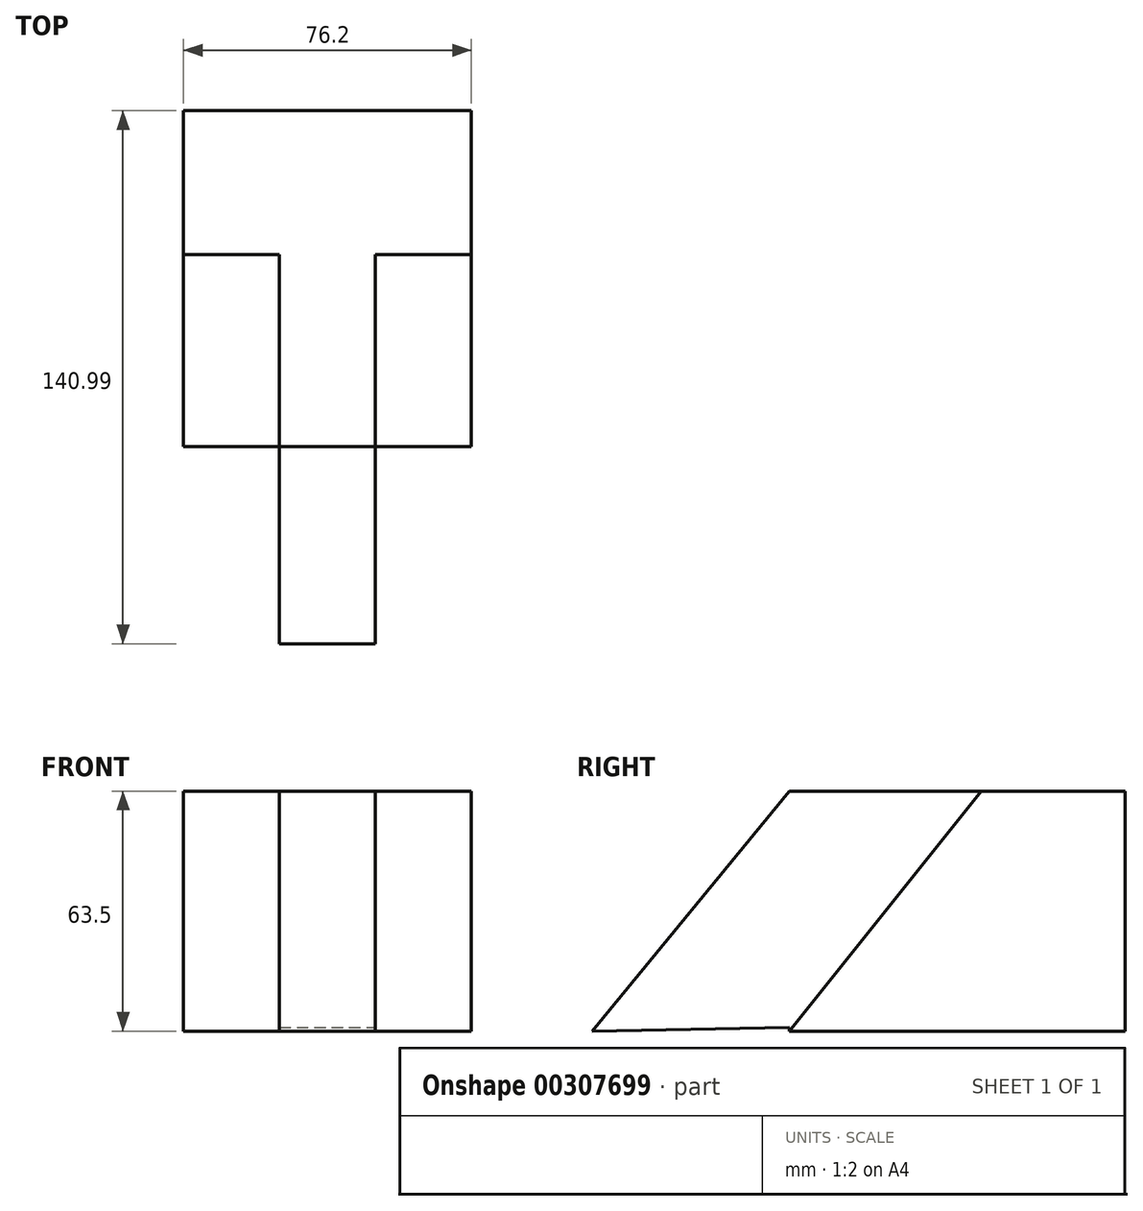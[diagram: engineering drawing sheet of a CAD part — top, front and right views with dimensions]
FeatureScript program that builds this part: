
annotation { "Feature Type Name" : "Feature", "Feature Type Description" : "" }
export const myFeature = defineFeature(function(context is Context, id is Id, definition is map)
    precondition{}
    {
        {
            var Q0;
            Q0=qCreatedBy(makeId("Top.planeOp"),FACE);
            var sketch = newSketch(context, id + "F0", { "sketchPlane" : qUnion([Q0])});
            skLineSegment(sketch, "E0", {"start": v(-45.15, 67.38) * mm, "end": v(31.05, 67.38) * mm});
            skLineSegment(sketch, "E1", {"start": v(31.05, 67.38) * mm, "end": v(31.05, 29.28) * mm});
            skLineSegment(sketch, "E2", {"start": v(31.05, 29.28) * mm, "end": v(5.65, 29.28) * mm});
            skLineSegment(sketch, "E3", {"start": v(5.65, 29.28) * mm, "end": v(5.65, -21.52) * mm});
            skLineSegment(sketch, "E4", {"start": v(5.65, -21.52) * mm, "end": v(-19.75, -21.52) * mm});
            skLineSegment(sketch, "E5", {"start": v(-19.75, -21.52) * mm, "end": v(-19.75, 29.28) * mm});
            skLineSegment(sketch, "E6", {"start": v(-19.75, 29.28) * mm, "end": v(-45.15, 29.28) * mm});
            skLineSegment(sketch, "E7", {"start": v(-45.15, 29.28) * mm, "end": v(-45.15, 67.38) * mm});
            skSolve(sketch);
        }
        {
            var Q0;
            Q0=makeQuery(id+"F0.imprint","IMPRINT",FACE,{"disambiguationData":[TD([[makeQuery(id+"F0.imprint","IMPRINT",EDGE,{"derivedFrom":sQuery(id+"F0.wireOp",EDGE,"E0")}),-1.0]])]});
            extrude(context, id + "F1", {"entities" : qUnion([Q0]), "depth" : 63.5 * mm});
        }
        {
            var Q0;
            Q0=makeQuery(id+"F1.opExtrude","SWEPT_FACE",FACE,{"disambiguationData":[OSD([sQuery(id+"F0.wireOp",EDGE,"E3")])]});
            var sketch = newSketch(context, id + "F2", { "sketchPlane" : qUnion([Q0])});
            skLineSegment(sketch, "E8", {"start": v(29.28, 63.5) * mm, "end": v(-21.52, 0) * mm});
            skLineSegment(sketch, "E9", {"start": v(-21.52, 0) * mm, "end": v(29.28, 0) * mm});
            skLineSegment(sketch, "E10", {"start": v(29.28, 0) * mm, "end": v(29.28, 63.5) * mm});
            skSolve(sketch);
        }
        {
            var Q0;
            Q0=makeQuery(id+"F2.imprint","IMPRINT",FACE,{"disambiguationData":[TD([[makeQuery(id+"F2.imprint","IMPRINT",EDGE,{"derivedFrom":sQuery(id+"F2.wireOp",EDGE,"E8")}),1.0]])]});
            extrude(context, id + "F3", {"entities" : qUnion([Q0]), "operationType" : NewBodyOperationType.ADD, "depth" : 25.4 * mm});
        }
        {
            var Q0;
            Q0=makeQuery(id+"F1.opExtrude","SWEPT_FACE",FACE,{"disambiguationData":[OSD([sQuery(id+"F0.wireOp",EDGE,"E3")])]});
            var sketch = newSketch(context, id + "F4", { "sketchPlane" : qUnion([Q0])});
            skLineSegment(sketch, "E11", {"start": v(-21.52, 63.5) * mm, "end": v(-73.61, 0) * mm});
            skLineSegment(sketch, "E12", {"start": v(-73.61, 0) * mm, "end": v(-21.52, 0.95) * mm});
            skLineSegment(sketch, "E13", {"start": v(-21.52, 0.95) * mm, "end": v(-21.52, 63.5) * mm});
            skSolve(sketch);
        }
        {
            var Q0;
            Q0=makeQuery(id+"F4.imprint","IMPRINT",FACE,{"disambiguationData":[TD([[makeQuery(id+"F4.imprint","IMPRINT",EDGE,{"derivedFrom":sQuery(id+"F4.wireOp",EDGE,"E11")}),1.0]])]});
            extrude(context, id + "F5", {"entities" : qUnion([Q0]), "operationType" : NewBodyOperationType.ADD, "oppositeDirection" : true, "depth" : 25.4 * mm});
        }
        {
            var Q0;
            Q0=makeQuery(id+"F5.boolean.opBoolean","MERGE",FACE,{"derivedFrom":[makeQuery(id+"F1.opExtrude","SWEPT_FACE",FACE,{"disambiguationData":[OSD([sQuery(id+"F0.wireOp",EDGE,"E5")])]}),makeQuery(id+"F5.opExtrude","CAP_FACE",FACE,{"disambiguationData":[OSD([sQuery(id+"F4.wireOp",EDGE,"E11"),sQuery(id+"F4.wireOp",EDGE,"E12"),sQuery(id+"F4.wireOp",EDGE,"E13")])],"isStart":false})]});
            var sketch = newSketch(context, id + "F6", { "sketchPlane" : qUnion([Q0])});
            skLineSegment(sketch, "E14", {"start": v(-29.28, 63.5) * mm, "end": v(21.52, 0) * mm});
            skLineSegment(sketch, "E15", {"start": v(21.52, 0) * mm, "end": v(-29.28, 0) * mm});
            skLineSegment(sketch, "E16", {"start": v(-29.28, 0) * mm, "end": v(-29.28, 63.5) * mm});
            skSolve(sketch);
        }
        {
            var Q0;
            Q0 = qSketchRegion(id + "F6", true);
            extrude(context, id + "F7", {"entities" : qUnion([Q0]), "operationType" : NewBodyOperationType.ADD, "depth" : 25.4 * mm});
        }
    });
